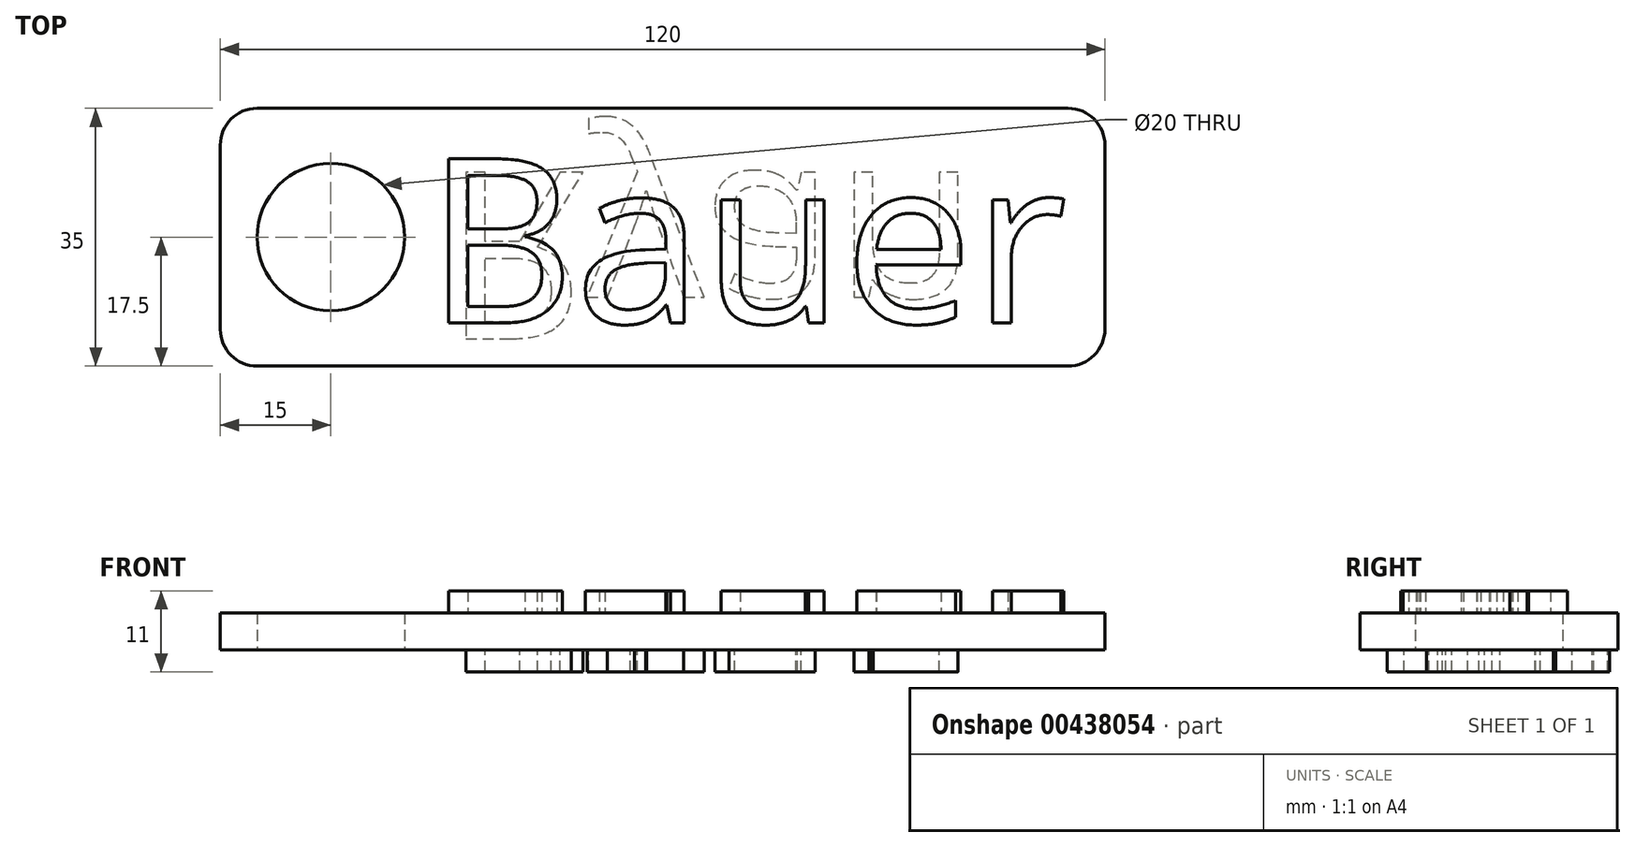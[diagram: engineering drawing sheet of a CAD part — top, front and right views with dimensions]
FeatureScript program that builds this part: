
annotation { "Feature Type Name" : "Feature", "Feature Type Description" : "" }
export const myFeature = defineFeature(function(context is Context, id is Id, definition is map)
    precondition{}
    {
        {
            var Q0;
            Q0=qCreatedBy(makeId("Top.planeOp"),FACE);
            var sketch = newSketch(context, id + "F0", { "sketchPlane" : qUnion([Q0])});
            skLineSegment(sketch, "E0.bottom", {"start": v(60, 17.5) * mm, "end": v(-60, 17.5) * mm});
            skLineSegment(sketch, "E0.top", {"start": v(60, -17.5) * mm, "end": v(-60, -17.5) * mm});
            skLineSegment(sketch, "E0.left", {"start": v(60, 17.5) * mm, "end": v(60, -17.5) * mm});
            skLineSegment(sketch, "E0.right", {"start": v(-60, 17.5) * mm, "end": v(-60, -17.5) * mm});
            skPoint(sketch, "E0.middle", {"position": v(0, 0) * mm});
            skCircle(sketch, "E1", {"center": v(-45, 0) * mm, "radius": 10 * mm});
            skSolve(sketch);
        }
        {
            var Q0;
            Q0=makeQuery(id+"F0.imprint","IMPRINT",FACE,{"disambiguationData":[TD([[makeQuery(id+"F0.imprint","IMPRINT",EDGE,{"derivedFrom":sQuery(id+"F0.wireOp",EDGE,"E0.bottom")}),1.0]])]});
            extrude(context, id + "F1", {"entities" : qUnion([Q0]), "depth" : 5 * mm});
        }
        {
            var Q0;
            Q0=makeQuery(id+"F1.opExtrude","SWEPT_EDGE",EDGE,{"disambiguationData":[OSD([sQuery(id+"F0.wireOp",EDGE,"E0.top"),sQuery(id+"F0.wireOp",EDGE,"E0.right")])]});
            var Q1;
            Q1=makeQuery(id+"F1.opExtrude","SWEPT_EDGE",EDGE,{"disambiguationData":[OSD([sQuery(id+"F0.wireOp",EDGE,"E0.top"),sQuery(id+"F0.wireOp",EDGE,"E0.left")])]});
            var Q2;
            Q2=makeQuery(id+"F1.opExtrude","SWEPT_EDGE",EDGE,{"disambiguationData":[OSD([sQuery(id+"F0.wireOp",EDGE,"E0.bottom"),sQuery(id+"F0.wireOp",EDGE,"E0.left")])]});
            var Q3;
            Q3=makeQuery(id+"F1.opExtrude","SWEPT_EDGE",EDGE,{"disambiguationData":[OSD([sQuery(id+"F0.wireOp",EDGE,"E0.bottom"),sQuery(id+"F0.wireOp",EDGE,"E0.right")])]});
            fillet(context, id + "F2", {"entities" : qUnion([Q0, Q1, Q2, Q3]), "radius" : 5 * mm, "tangentPropagation" : true, "allowEdgeOverflow" : false});
        }
        {
            var Q0;
            Q0=makeQuery(id+"F1.opExtrude","CAP_FACE",FACE,{"disambiguationData":[OSD([sQuery(id+"F0.wireOp",EDGE,"E0.bottom"),sQuery(id+"F0.wireOp",EDGE,"E0.top"),sQuery(id+"F0.wireOp",EDGE,"E0.left"),sQuery(id+"F0.wireOp",EDGE,"E0.right"),sQuery(id+"F0.wireOp",EDGE,"E1")])],"isStart":false});
            var sketch = newSketch(context, id + "F3", { "sketchPlane" : qUnion([Q0])});
            skText(sketch, "E2", { "text": "Bauer", "fontName": "OpenSans-Regular.ttf"});
            const initialGuessF3  = {"E2": [-0.0321, -0.01163, 1, 0, 0.02246]};
            skSetInitialGuess(sketch, initialGuessF3);
            skSolve(sketch);
        }
        {
            var Q0;
            Q0 = qSketchRegion(id + "F3", true);
            extrude(context, id + "F4", {"entities" : qUnion([Q0]), "operationType" : NewBodyOperationType.ADD, "depth" : 3 * mm});
        }
        {
            var Q0;
            Q0=makeQuery(id+"F1.opExtrude","CAP_FACE",FACE,{"disambiguationData":[OSD([sQuery(id+"F0.wireOp",EDGE,"E0.bottom"),sQuery(id+"F0.wireOp",EDGE,"E0.top"),sQuery(id+"F0.wireOp",EDGE,"E0.left"),sQuery(id+"F0.wireOp",EDGE,"E0.right"),sQuery(id+"F0.wireOp",EDGE,"E1")])],"isStart":true});
            var sketch = newSketch(context, id + "F5", { "sketchPlane" : qUnion([Q0])});
            skText(sketch, "E3", { "text": "Ryan", "fontName": "OpenSans-Regular.ttf"});
            const initialGuessF5  = {"E3": [-0.0298, -0.00878, 1, 0, 0.02275]};
            skSetInitialGuess(sketch, initialGuessF5);
            skSolve(sketch);
        }
        {
            var Q0;
            Q0 = qSketchRegion(id + "F5", true);
            extrude(context, id + "F6", {"entities" : qUnion([Q0]), "operationType" : NewBodyOperationType.ADD, "depth" : 3 * mm});
        }
    });
